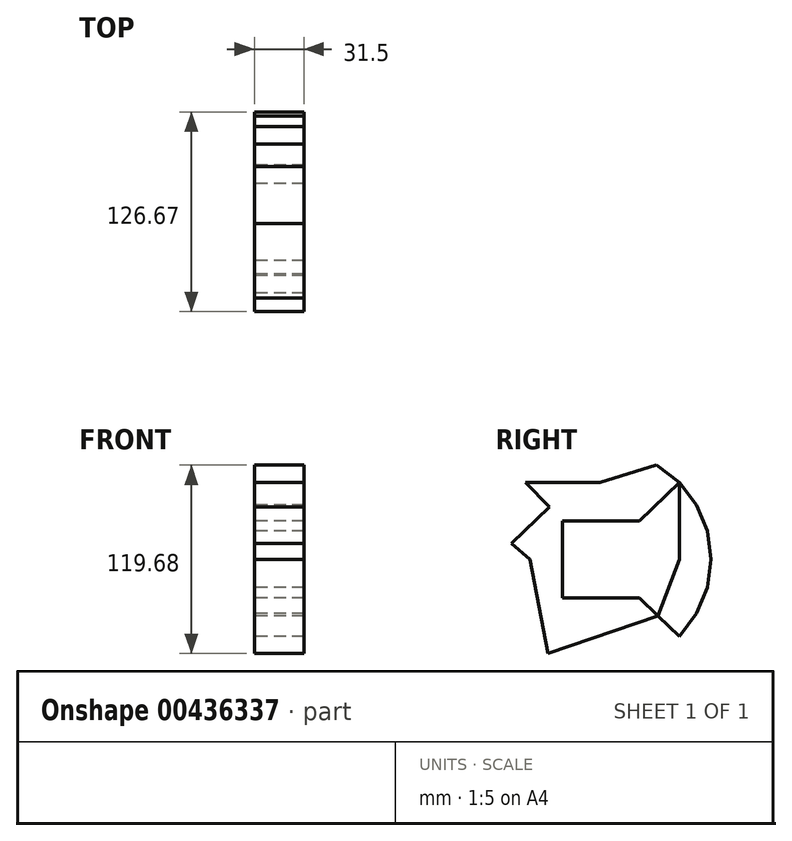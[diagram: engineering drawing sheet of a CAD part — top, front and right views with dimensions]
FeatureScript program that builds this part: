
annotation { "Feature Type Name" : "Feature", "Feature Type Description" : "" }
export const myFeature = defineFeature(function(context is Context, id is Id, definition is map)
    precondition{}
    {
        {
            var Q0;
            Q0=qCreatedBy(makeId("Right.planeOp"),FACE);
            var sketch = newSketch(context, id + "F0", { "sketchPlane" : qUnion([Q0])});
            skCircle(sketch, "E0.cCircle", {"center": v(1.62, 0) * mm, "radius": 69.1 * mm, "construction": true});
            skLineSegment(sketch, "E0.0", {"start": v(-67.48, 0) * mm, "end": v(-65.12, 17.88) * mm});
            skLineSegment(sketch, "E0.1", {"start": v(-65.12, 17.88) * mm, "end": v(-58.22, 34.55) * mm});
            skLineSegment(sketch, "E0.2", {"start": v(-58.22, 34.55) * mm, "end": v(-47.24, 48.86) * mm});
            skLineSegment(sketch, "E0.3", {"start": v(-47.24, 48.86) * mm, "end": v(-32.93, 59.84) * mm});
            skLineSegment(sketch, "E0.4", {"start": v(-32.93, 59.84) * mm, "end": v(-16.27, 66.74) * mm});
            skLineSegment(sketch, "E0.5", {"start": v(-16.27, 66.74) * mm, "end": v(1.62, 69.1) * mm});
            skLineSegment(sketch, "E0.6", {"start": v(1.62, 69.1) * mm, "end": v(19.5, 66.74) * mm});
            skLineSegment(sketch, "E0.7", {"start": v(19.5, 66.74) * mm, "end": v(36.16, 59.84) * mm});
            skLineSegment(sketch, "E0.8", {"start": v(36.16, 59.84) * mm, "end": v(50.48, 48.86) * mm});
            skLineSegment(sketch, "E0.9", {"start": v(50.48, 48.86) * mm, "end": v(61.46, 34.55) * mm});
            skLineSegment(sketch, "E0.10", {"start": v(61.46, 34.55) * mm, "end": v(68.36, 17.88) * mm});
            skLineSegment(sketch, "E0.11", {"start": v(68.36, 17.88) * mm, "end": v(70.71, 0) * mm});
            skLineSegment(sketch, "E0.12", {"start": v(70.71, 0) * mm, "end": v(68.36, -17.88) * mm});
            skLineSegment(sketch, "E0.13", {"start": v(68.36, -17.88) * mm, "end": v(61.46, -34.55) * mm});
            skLineSegment(sketch, "E0.14", {"start": v(61.46, -34.55) * mm, "end": v(50.48, -48.86) * mm});
            skLineSegment(sketch, "E0.15", {"start": v(50.48, -48.86) * mm, "end": v(36.16, -59.84) * mm});
            skLineSegment(sketch, "E0.16", {"start": v(36.16, -59.84) * mm, "end": v(19.5, -66.74) * mm});
            skLineSegment(sketch, "E0.17", {"start": v(19.5, -66.74) * mm, "end": v(1.62, -69.1) * mm});
            skLineSegment(sketch, "E0.18", {"start": v(1.62, -69.1) * mm, "end": v(-16.27, -66.74) * mm});
            skLineSegment(sketch, "E0.19", {"start": v(-16.27, -66.74) * mm, "end": v(-32.93, -59.84) * mm});
            skLineSegment(sketch, "E0.20", {"start": v(-32.93, -59.84) * mm, "end": v(-47.24, -48.86) * mm});
            skLineSegment(sketch, "E0.21", {"start": v(-47.24, -48.86) * mm, "end": v(-58.22, -34.55) * mm});
            skLineSegment(sketch, "E0.22", {"start": v(-58.22, -34.55) * mm, "end": v(-65.12, -17.88) * mm});
            skLineSegment(sketch, "E0.23", {"start": v(-65.12, -17.88) * mm, "end": v(-67.48, 0) * mm});
            skLineSegment(sketch, "E1", {"start": v(0, 0) * mm, "end": v(-47.24, 48.86) * mm});
            skLineSegment(sketch, "E2", {"start": v(0, 0) * mm, "end": v(-47.24, -48.86) * mm});
            skLineSegment(sketch, "E3", {"start": v(0, 0) * mm, "end": v(50.48, 48.86) * mm});
            skLineSegment(sketch, "E4", {"start": v(0, 0) * mm, "end": v(50.48, -48.86) * mm});
            skLineSegment(sketch, "E5", {"start": v(-23.62, 24.43) * mm, "end": v(25.24, 24.43) * mm});
            skLineSegment(sketch, "E6", {"start": v(25.24, 24.43) * mm, "end": v(25.24, -24.43) * mm});
            skLineSegment(sketch, "E7", {"start": v(25.24, -24.43) * mm, "end": v(-23.62, -24.43) * mm});
            skLineSegment(sketch, "E8", {"start": v(-23.62, -24.43) * mm, "end": v(-23.62, 24.43) * mm});
            skLineSegment(sketch, "E9", {"start": v(0, 48.86) * mm, "end": v(-47.24, 48.86) * mm});
            skLineSegment(sketch, "E10", {"start": v(0, 48.86) * mm, "end": v(36.16, 59.84) * mm});
            skLineSegment(sketch, "E11", {"start": v(50.48, 48.86) * mm, "end": v(50.48, 0) * mm});
            skLineSegment(sketch, "E12", {"start": v(50.48, 0) * mm, "end": v(37.09, -35.9) * mm});
            skLineSegment(sketch, "E13", {"start": v(37.09, -35.9) * mm, "end": v(-32.93, -59.84) * mm});
            skLineSegment(sketch, "E14", {"start": v(-32.93, -59.84) * mm, "end": v(-44.28, 0) * mm});
            skLineSegment(sketch, "E15", {"start": v(-44.28, 0) * mm, "end": v(-65.12, 17.88) * mm});
            skLineSegment(sketch, "E16", {"start": v(-32.06, 33.16) * mm, "end": v(-55.96, 10.02) * mm});
            skSolve(sketch);
        }
        {
            var Q0;
            {var subQ1=sQuery(id+"F0.wireOp",EDGE,"E0.8");Q0=makeQuery(id+"F0.imprint","IMPRINT",FACE,{"disambiguationData":[TD([[makeQuery(id+"F0.imprint","IMPRINT",EDGE,{"derivedFrom":subQ1}),-1.0]])]});}
            var Q1;
            {var subQ0=sQuery(id+"F0.wireOp",EDGE,"E7");Q1=makeQuery(id+"F0.imprint","IMPRINT",FACE,{"disambiguationData":[TD([[makeQuery(id+"F0.imprint","IMPRINT",EDGE,{"derivedFrom":subQ0}),1.0]])]});}
            var Q2;
            {var subQ0=sQuery(id+"F0.wireOp",EDGE,"E8");Q2=makeQuery(id+"F0.imprint","IMPRINT",FACE,{"disambiguationData":[TD([[makeQuery(id+"F0.imprint","IMPRINT",EDGE,{"derivedFrom":subQ0}),1.0]])]});}
            var Q3;
            Q3=makeQuery(id+"F0.imprint","IMPRINT",FACE,{"disambiguationData":[TD([[makeQuery(id+"F0.imprint","IMPRINT",EDGE,{"derivedFrom":sQuery(id+"F0.wireOp",EDGE,"E0.9")}),-1.0]])]});
            extrude(context, id + "F1", {"entities" : qUnion([Q0, Q1, Q2, Q3]), "depth" : 31.5 * mm});
        }
    });
